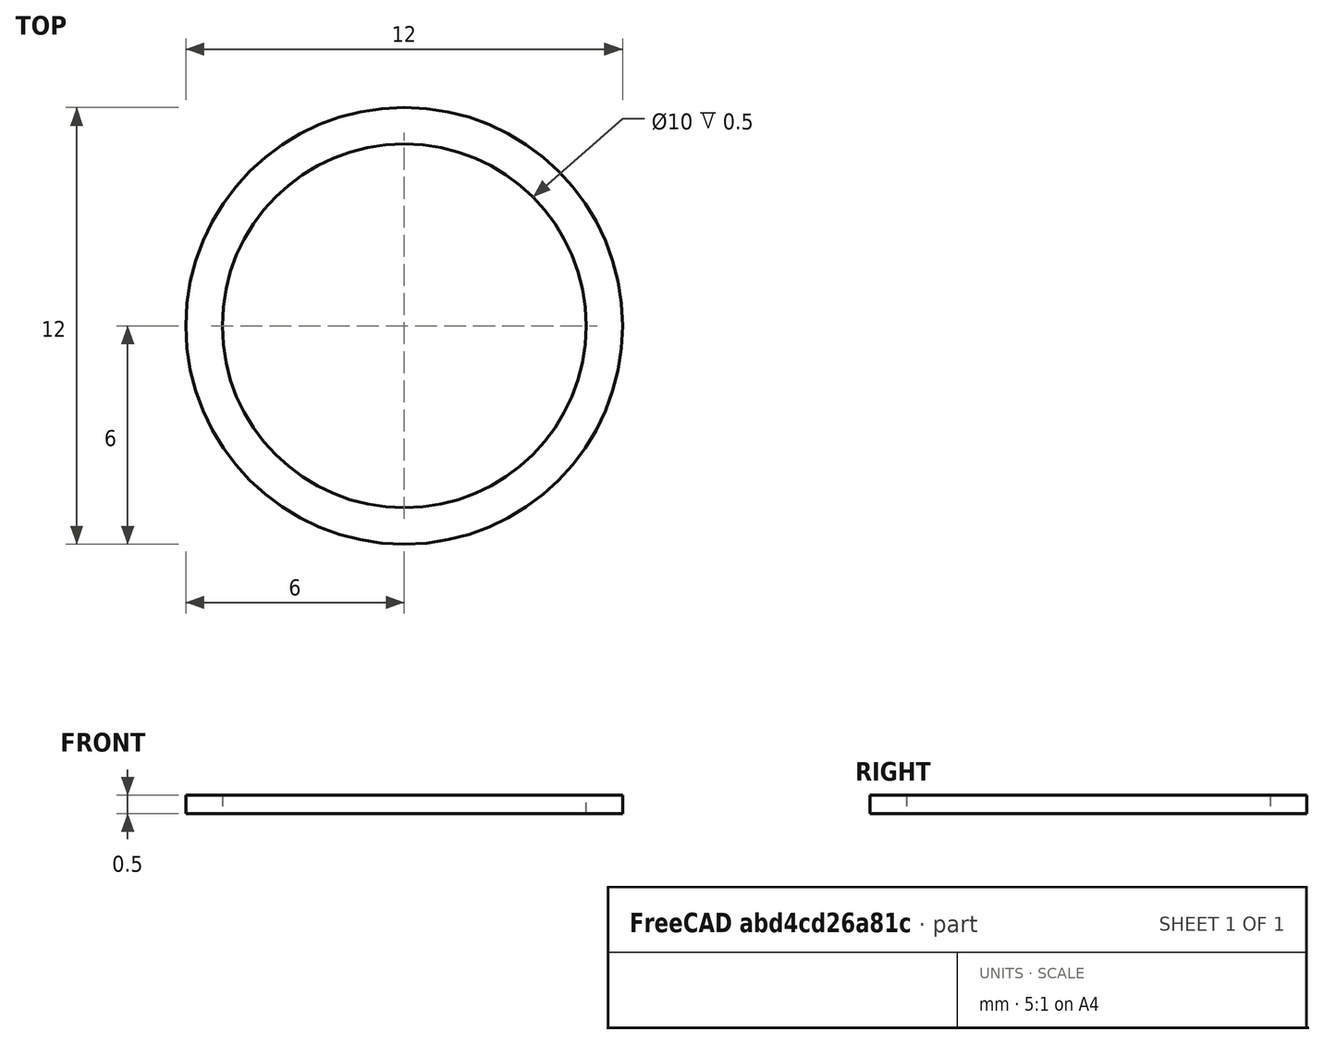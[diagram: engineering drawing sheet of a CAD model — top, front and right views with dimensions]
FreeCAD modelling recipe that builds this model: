
FCSTD DOCUMENT  (FreeCAD 2023.131R26244 +5365 (Git))
Label: bearing_spacer
License: All rights reserved
LicenseURL: http://en.wikipedia.org/wiki/All_rights_reserved
objects: Sketcher::SketchObject×1, PartDesign::Pad×1, PartDesign::Body×1
note: 6 computed .brp shape members not serialized (recipe doc carries the construction recipe); baked Part::Feature solids carry a one-line shape summary decoded from their .brp

FEATURE [Sketcher::SketchObject] Sketch
  ArcFitTolerance = 1e-06
  AttachmentSupport = -> [XY_Plane]
  ExternalBSplineMaxDegree = 5
  ExternalBSplineTolerance = 0.0001
  FixShape = 1
  FullyConstrained = true
  InternalTolerance = 1e-06
  InvalidShape = false
  MakeInternals = false
  MapMode = 5
  Support = -> [XY_Plane]
  TreeRank = 11
  ValidateShape = false
  sketch-geometry (2):
    g0: Circle CenterX=0 CenterY=0 CenterZ=0 NormalX=0 NormalY=0 NormalZ=1 AngleXU=0 Radius=5
    g1: Circle CenterX=0 CenterY=0 CenterZ=0 NormalX=0 NormalY=0 NormalZ=1 AngleXU=0 Radius=6
  constraints (4):
    c: Coincident(g0,g-1)
    c: Coincident(g1,g0)
    c: Diameter(g0) = 10
    c: Diameter(g1) = 12
FEATURE [PartDesign::Pad] Pad
  AddSubType = 0
  AlongSketchNormal = false
  AutoTaperInnerAngle = true
  CheckUpToFaceLimits = true
  ClaimChildren = false
  Direction = (0,0,1)
  Fit = 0
  FitJoin = 0
  FixShape = 1
  InnerFit = 0
  InnerFitJoin = 0
  InvalidShape = false
  Length = 0.5
  Length2 = 100
  Linearize = true
  NewSolid = false
  Profile = -> Sketch
  Refine = true
  Suppress = false
  TaperInnerAngle = 0
  TaperInnerAngleRev = 0
  TreeRank = 12
  Type = 0
  ValidateShape = false
  _ProfileBasedVersion = 1
FEATURE [PartDesign::Body] Body  label="spacer"
  AutoGroupSolids = false
  ClaimAllChildren = false
  ExportMode = 0
  FixShape = 1
  Group = -> [Sketch,Pad]
  InvalidShape = false
  Origin = -> Origin
  Tip = -> Pad
  TreeRank = 10
  ValidateShape = false
  _ExportChildren = -> [Pad]
  _GroupVersion = 1
